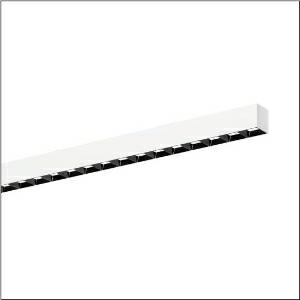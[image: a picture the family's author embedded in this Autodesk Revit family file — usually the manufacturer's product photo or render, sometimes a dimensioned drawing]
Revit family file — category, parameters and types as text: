
# Revit family: silica_r__21_51mx22da44wb_17fd
name_source: partatom
category: Lighting Fixtures
units: mm (PartAtom-declared; Revit-internal decimal feet)

## family parameters
Cut with Voids When Loaded = No
Host = Face
Light Source = No
Part Type = Normal
Room Calculation Point = No
Round Connector Dimension = Use Diameter
Shared = No

## types (1)
- --- (1 x LED, 4320 lm, 25.6 W, 4000K)
    Apparent Load = 26 VA
    CIE Flux Codes = 86 100 100 100 100
    Color Rendering = 80
    Color Temperature = 4000K
    Default Elevation = 1800 mm
    Description = Silica® 21, office luminaire, primary light control with darklight reflector, of PMMA, black, CAT 2 (L<= 3000cd/m²), light emission: direct distribution, primary light characteristic: symmetric, installation type: surface-mounted, LED, rated luminous flux: 4.320lm, luminous efficacy: 169lm/W, light colour: 840, colour temperature: 4000K, control gear: DALI 2, with terminal, 3+2-pole, max. 2.5mm², mains connection: 220..240V, AC, 50/60Hz, rated input power: 25.6W, luminaire housing, of aluminium, traffic white (RAL 9016), length: 1.204mm, width: 53mm, height: 53mm, protection rating (complete): IP20, insulation class (complete): insulation class I (protective earthing), certification: CE, permissible operating ambient temperature: 0..+35°C, standard: EN 50419, packaging unit: 1 piece
    Height = 53 mm
    Lamp = 1 x LED
    Lamp Light Flux = 4320 lm
    Lamp Power = 25.6 W
    Lamp count = 1
    Length = 1204 mm
    Luminous efficacy = 169 lm/W
    Manufacturer = Siteco
    ModVariant = No
    Model = 51MX22DA44WB
    Mounting Place = Ceiling
    Mounting Type = Surface mounted
    Number of Poles = 1
    OnlyDefault = Yes
    Power Factor = 1
    Product Name = Silica® 21
    Product group = office luminaire | ceiling mounted
    ProductGroupID = 302
    Protection Class = Protection class I
    Protection Degree = IP 20
    RLX_Detail_Level = 1
    RLX_Emergency_Light_Flux = 0 lm
    RLX_Emergency_Type = 0
    RLX_Emergency_Type_DB = No
    RlxData = <blob elided: 41309 chars, md5=d009342e>
    Socket = socket
    Standby Power = 0 W
    System Light Flux = 4320 lm
    System Power = 26 W
    Type Comments = factory setting: luminous flux: 100 % | dim-lin: 254 | 367 mA
    Type Image = l_1335873.jpg
    URL = http://relux.com
    VarID = @adj_008877
    Voltage = 0 V
    Weight = 0.00 kg
    Width = 53 mm

## geometry (parser evidence)
native form markers: Blend x4, Sweep x11
no freeform markers — native parametric forms only
